# Revit family: 3100.205  Roof Drain
name_source: partatom
category: Plumbing Fixtures
revit_build: Autodesk Revit 2016 (Build: 20150714_1515(x64)
units: mm (PartAtom-declared; Revit-internal decimal feet)

## family parameters
Always vertical = Yes
Cut with Voids When Loaded = No
OmniClass Number = 23.45.00.00
OmniClass Title = Sanitary, Laundry, and Cleaning Equipment
Part Type = Normal
Room Calculation Point = No
Round Connector Dimension = Use Diameter
Shared = No
Work Plane-Based = No

## types (2) — shared parameters
CW Connection = No
Connector Location = 75 mm
HW Connection = No
Manufacturer = Aquanight Industries Ltd
Model = 3100.205
URL = www.aquaknight.co.nz
Vent Connection = Yes
Waste Connection = Yes

## per-type parameters (varying)
| type | Connector Size | Description |
| 3100.205 DN80 | 80 mm  [stored 0.262467 ft] | Roof Drain SD HF BE80 DN100 x 80 |
| 3100.205 DN100 | 100 mm  [stored 0.328084 ft] | Roof Drain SD HF BE80 DN100 x100 |

note: [stored X ft] marks values corroborated as IEEE doubles in the binary element streams (Revit-internal decimal feet)

## geometry (parser evidence)
native form markers: Sweep x5
no freeform markers — native parametric forms only
